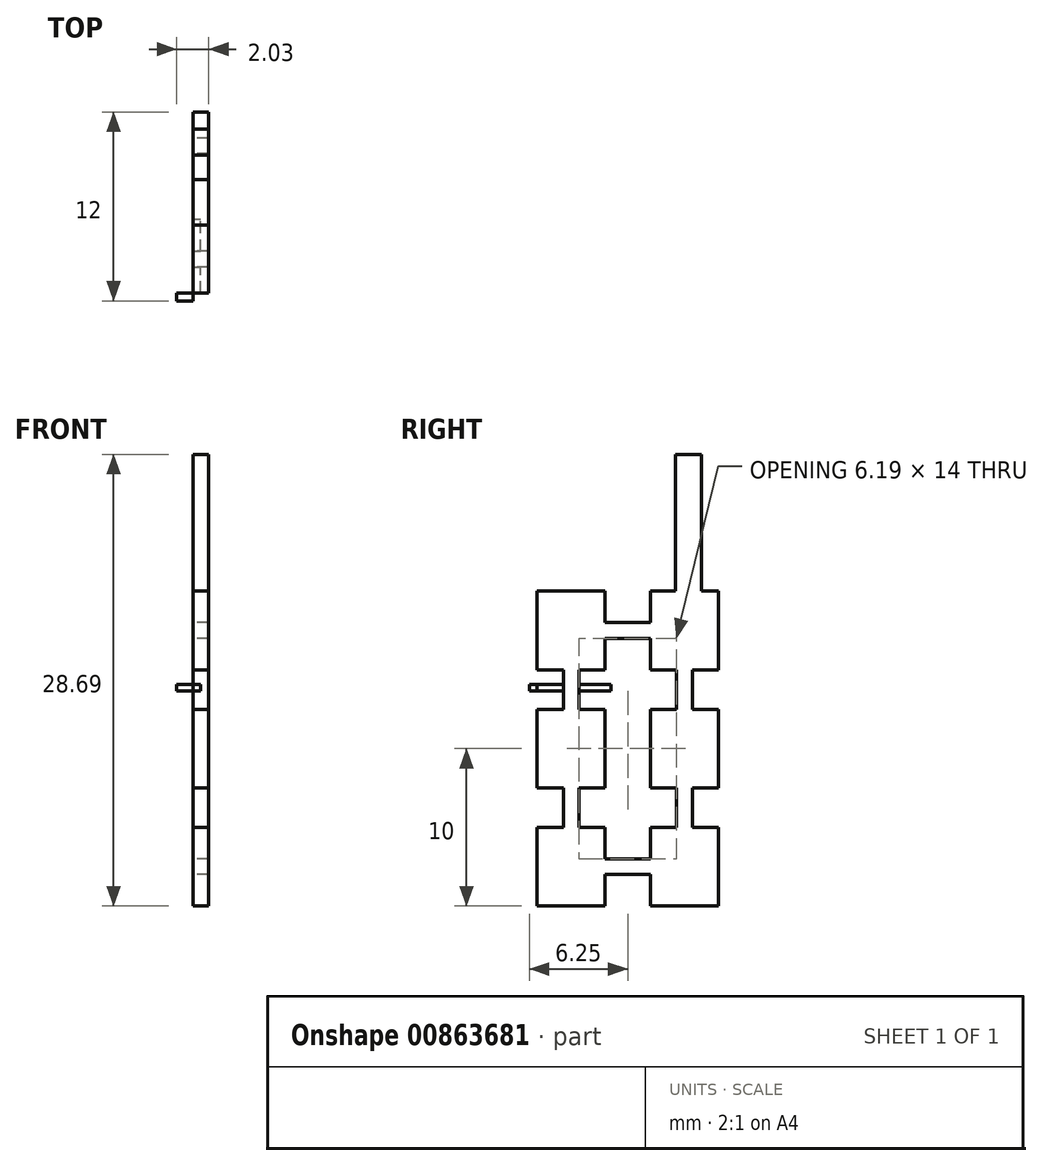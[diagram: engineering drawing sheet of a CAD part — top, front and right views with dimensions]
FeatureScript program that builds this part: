
annotation { "Feature Type Name" : "Feature", "Feature Type Description" : "" }
export const myFeature = defineFeature(function(context is Context, id is Id, definition is map)
    precondition{}
    {
        {
            var Q0;
            Q0=qCreatedBy(makeId("Right.planeOp"),FACE);
            var sketch = newSketch(context, id + "F0", { "sketchPlane" : qUnion([Q0])});
            skLineSegment(sketch, "E0.top", {"start": v(0, -11.5) * mm, "end": v(4.31, -11.5) * mm});
            skPoint(sketch, "E1.end.orphan", {"position": v(2.16, -7.19) * mm});
            skLineSegment(sketch, "E2", {"start": v(0, -11.5) * mm, "end": v(0, -6.5) * mm});
            skLineSegment(sketch, "E3", {"start": v(0, -6.5) * mm, "end": v(4.31, -6.5) * mm});
            skLineSegment(sketch, "E4.0", {"start": v(0, -4) * mm, "end": v(4.31, -4) * mm});
            skLineSegment(sketch, "E5.0", {"start": v(0, 1) * mm, "end": v(4.31, 1) * mm});
            skLineSegment(sketch, "E6.0", {"start": v(0, 3.5) * mm, "end": v(4.31, 3.5) * mm});
            skLineSegment(sketch, "E7.0", {"start": v(0, 8.5) * mm, "end": v(4.31, 8.5) * mm});
            skLineSegment(sketch, "E8", {"start": v(0, 8.5) * mm, "end": v(0, 3.5) * mm});
            skLineSegment(sketch, "E9", {"start": v(0, 1) * mm, "end": v(0, -4) * mm});
            skLineSegment(sketch, "E10", {"start": v(4.31, 8.5) * mm, "end": v(4.31, 3.5) * mm});
            skLineSegment(sketch, "E11", {"start": v(4.31, 1) * mm, "end": v(4.31, -4) * mm});
            skLineSegment(sketch, "E12.MirrorCS", {"start": v(11.5, 8.5) * mm, "end": v(7.19, 8.5) * mm});
            skLineSegment(sketch, "E13.MirrorCS", {"start": v(11.5, 8.5) * mm, "end": v(11.5, 3.5) * mm});
            skLineSegment(sketch, "E14.MirrorCS", {"start": v(11.5, 3.5) * mm, "end": v(7.19, 3.5) * mm});
            skLineSegment(sketch, "E15.MirrorCS", {"start": v(7.19, 8.5) * mm, "end": v(7.19, 3.5) * mm});
            skLineSegment(sketch, "E16.MirrorCS", {"start": v(11.5, 1) * mm, "end": v(7.19, 1) * mm});
            skLineSegment(sketch, "E17.MirrorCS", {"start": v(11.5, 1) * mm, "end": v(11.5, -4) * mm});
            skLineSegment(sketch, "E18.MirrorCS", {"start": v(11.5, -4) * mm, "end": v(7.19, -4) * mm});
            skLineSegment(sketch, "E19.MirrorCS", {"start": v(7.19, 1) * mm, "end": v(7.19, -4) * mm});
            skLineSegment(sketch, "E20.MirrorCS", {"start": v(11.5, -6.5) * mm, "end": v(7.19, -6.5) * mm});
            skLineSegment(sketch, "E21.MirrorCS", {"start": v(11.5, -11.5) * mm, "end": v(11.5, -6.5) * mm});
            skLineSegment(sketch, "E22.MirrorCS", {"start": v(11.5, -11.5) * mm, "end": v(7.19, -11.5) * mm});
            skLineSegment(sketch, "E23.MirrorCS", {"start": v(7.19, -7.19) * mm, "end": v(7.19, -11.5) * mm});
            skLineSegment(sketch, "E24.MirrorCS", {"start": v(7.19, -6.5) * mm, "end": v(7.19, -7.19) * mm});
            skLineSegment(sketch, "E25", {"start": v(4.31, -6.5) * mm, "end": v(4.31, -11.5) * mm});
            skLineSegment(sketch, "E26.0", {"start": v(4.31, -9.5) * mm, "end": v(7.19, -9.5) * mm});
            skLineSegment(sketch, "E27.0", {"start": v(4.31, -8.5) * mm, "end": v(7.19, -8.5) * mm});
            skLineSegment(sketch, "E28.0", {"start": v(8.84, -4) * mm, "end": v(8.84, -6.5) * mm});
            skLineSegment(sketch, "E29.0", {"start": v(9.84, -4) * mm, "end": v(9.84, -6.5) * mm});
            skLineSegment(sketch, "E30.0", {"start": v(1.66, -4) * mm, "end": v(1.66, -6.5) * mm});
            skLineSegment(sketch, "E31.0", {"start": v(2.66, -4) * mm, "end": v(2.66, -6.5) * mm});
            skLineSegment(sketch, "E32.0", {"start": v(1.66, 3.5) * mm, "end": v(1.66, 1) * mm});
            skLineSegment(sketch, "E33.0", {"start": v(2.66, 3.5) * mm, "end": v(2.66, 1) * mm});
            skLineSegment(sketch, "E34.0", {"start": v(4.31, 5.5) * mm, "end": v(7.19, 5.5) * mm});
            skLineSegment(sketch, "E35.0", {"start": v(4.31, 6.5) * mm, "end": v(7.19, 6.5) * mm});
            skLineSegment(sketch, "E36.0", {"start": v(8.84, 3.5) * mm, "end": v(8.84, 1) * mm});
            skLineSegment(sketch, "E37.0", {"start": v(9.84, 3.5) * mm, "end": v(9.84, 1) * mm});
            skPoint(sketch, "E38.end.orphan", {"position": v(2.16, -6.5) * mm});
            skPoint(sketch, "E38.start.orphan", {"position": v(2.16, -4) * mm});
            skPoint(sketch, "E39.start.orphan", {"position": v(4.31, -9) * mm});
            skPoint(sketch, "E40.end.orphan", {"position": v(9.34, -6.5) * mm});
            skPoint(sketch, "E40.start.orphan", {"position": v(9.34, -4) * mm});
            skPoint(sketch, "E41.end.orphan", {"position": v(9.34, 1) * mm});
            skPoint(sketch, "E41.start.orphan", {"position": v(9.34, 3.5) * mm});
            skPoint(sketch, "E42.end.orphan", {"position": v(7.19, 6) * mm});
            skPoint(sketch, "E42.start.orphan", {"position": v(4.31, 6) * mm});
            skPoint(sketch, "E43.end.orphan", {"position": v(2.16, 1) * mm});
            skPoint(sketch, "E43.start.orphan", {"position": v(2.16, 3.5) * mm});
            skLineSegment(sketch, "E44", {"start": v(10.42, 8.5) * mm, "end": v(10.42, 17.2) * mm});
            skLineSegment(sketch, "E45", {"start": v(10.42, 17.2) * mm, "end": v(8.77, 17.2) * mm});
            skLineSegment(sketch, "E46", {"start": v(8.77, 17.2) * mm, "end": v(8.77, 8.5) * mm});
            skSolve(sketch);
        }
        {
            var Q0;
            {var subQ0=sQuery(id+"F0.wireOp",EDGE,"E7.0");Q0=makeQuery(id+"F0.imprint","IMPRINT",FACE,{"disambiguationData":[TD([[makeQuery(id+"F0.imprint","IMPRINT",EDGE,{"derivedFrom":subQ0}),-1.0]])]});}
            var Q1;
            {var subQ0=sQuery(id+"F0.wireOp",EDGE,"E32.0");Q1=makeQuery(id+"F0.imprint","IMPRINT",FACE,{"disambiguationData":[TD([[makeQuery(id+"F0.imprint","IMPRINT",EDGE,{"derivedFrom":subQ0}),1.0]])]});}
            var Q2;
            {var subQ0=sQuery(id+"F0.wireOp",EDGE,"E9");Q2=makeQuery(id+"F0.imprint","IMPRINT",FACE,{"disambiguationData":[TD([[makeQuery(id+"F0.imprint","IMPRINT",EDGE,{"derivedFrom":subQ0}),1.0]])]});}
            var Q3;
            {var subQ0=sQuery(id+"F0.wireOp",EDGE,"E30.0");Q3=makeQuery(id+"F0.imprint","IMPRINT",FACE,{"disambiguationData":[TD([[makeQuery(id+"F0.imprint","IMPRINT",EDGE,{"derivedFrom":subQ0}),1.0]])]});}
            var Q4;
            {var subQ7=sQuery(id+"F0.wireOp",EDGE,"E2");Q4=makeQuery(id+"F0.imprint","IMPRINT",FACE,{"disambiguationData":[TD([[makeQuery(id+"F0.imprint","IMPRINT",EDGE,{"derivedFrom":subQ7}),-1.0]])]});}
            var Q5;
            {var subQ0=sQuery(id+"F0.wireOp",EDGE,"E26.0");Q5=makeQuery(id+"F0.imprint","IMPRINT",FACE,{"disambiguationData":[TD([[makeQuery(id+"F0.imprint","IMPRINT",EDGE,{"derivedFrom":subQ0}),1.0]])]});}
            var Q6;
            {var subQ0=sQuery(id+"F0.wireOp",EDGE,"E21.MirrorCS");Q6=makeQuery(id+"F0.imprint","IMPRINT",FACE,{"disambiguationData":[TD([[makeQuery(id+"F0.imprint","IMPRINT",EDGE,{"derivedFrom":subQ0}),1.0]])]});}
            var Q7;
            {var subQ0=sQuery(id+"F0.wireOp",EDGE,"E28.0");Q7=makeQuery(id+"F0.imprint","IMPRINT",FACE,{"disambiguationData":[TD([[makeQuery(id+"F0.imprint","IMPRINT",EDGE,{"derivedFrom":subQ0}),1.0]])]});}
            var Q8;
            {var subQ0=sQuery(id+"F0.wireOp",EDGE,"E17.MirrorCS");Q8=makeQuery(id+"F0.imprint","IMPRINT",FACE,{"disambiguationData":[TD([[makeQuery(id+"F0.imprint","IMPRINT",EDGE,{"derivedFrom":subQ0}),-1.0]])]});}
            var Q9;
            {var subQ4=sQuery(id+"F0.wireOp",EDGE,"E12.MirrorCS");Q9=makeQuery(id+"F0.imprint","IMPRINT",FACE,{"disambiguationData":[TD([[makeQuery(id+"F0.imprint","IMPRINT",EDGE,{"derivedFrom":subQ4}),1.0]])]});}
            var Q10;
            {var subQ0=sQuery(id+"F0.wireOp",EDGE,"E34.0");Q10=makeQuery(id+"F0.imprint","IMPRINT",FACE,{"disambiguationData":[TD([[makeQuery(id+"F0.imprint","IMPRINT",EDGE,{"derivedFrom":subQ0}),1.0]])]});}
            var Q11;
            {var subQ0=sQuery(id+"F0.wireOp",EDGE,"E36.0");Q11=makeQuery(id+"F0.imprint","IMPRINT",FACE,{"disambiguationData":[TD([[makeQuery(id+"F0.imprint","IMPRINT",EDGE,{"derivedFrom":subQ0}),1.0]])]});}
            var Q12;
            {var subQ0=sQuery(id+"F0.wireOp",EDGE,"E44");Q12=makeQuery(id+"F0.imprint","IMPRINT",FACE,{"disambiguationData":[TD([[makeQuery(id+"F0.imprint","IMPRINT",EDGE,{"derivedFrom":subQ0}),1.0]])]});}
            extrude(context, id + "F1", {"entities" : qUnion([Q0, Q1, Q2, Q3, Q4, Q5, Q6, Q7, Q8, Q9, Q10, Q11, Q12]), "depth" : 1 * mm, "offsetDistance" : 25 * mm});
        }
        {
            var Q0;
            Q0=qCreatedBy(makeId("Right.planeOp"),FACE);
            var sketch = newSketch(context, id + "F2", { "sketchPlane" : qUnion([Q0])});
            skLineSegment(sketch, "E47.bottom", {"start": v(0, 2.58) * mm, "end": v(4.68, 2.58) * mm});
            skLineSegment(sketch, "E47.top", {"start": v(0, 2.17) * mm, "end": v(4.68, 2.17) * mm});
            skLineSegment(sketch, "E47.left", {"start": v(0, 2.58) * mm, "end": v(0, 2.17) * mm});
            skLineSegment(sketch, "E47.right", {"start": v(4.68, 2.58) * mm, "end": v(4.68, 2.17) * mm});
            skSolve(sketch);
        }
        {
            var Q0;
            Q0=makeQuery(id+"F2.imprint","IMPRINT",FACE,{"disambiguationData":[TD([[makeQuery(id+"F2.imprint","IMPRINT",EDGE,{"derivedFrom":sQuery(id+"F2.wireOp",EDGE,"E47.bottom")}),-1.0]])]});
            extrude(context, id + "F3", {"entities" : qUnion([Q0]), "operationType" : NewBodyOperationType.ADD, "depth" : .5 * mm, "offsetDistance" : 25 * mm});
        }
        {
            var Q0;
            Q0=qCreatedBy(makeId("Front.planeOp"),FACE);
            var sketch = newSketch(context, id + "F4", { "sketchPlane" : qUnion([Q0])});
            skLineSegment(sketch, "E48.0", {"start": v(0, 2.58) * mm, "end": v(0, 2.17) * mm});
            skLineSegment(sketch, "E49", {"start": v(0, 2.58) * mm, "end": v(-1.03, 2.58) * mm});
            skLineSegment(sketch, "E50", {"start": v(-1.03, 2.58) * mm, "end": v(-1.03, 2.17) * mm});
            skLineSegment(sketch, "E51", {"start": v(-1.03, 2.17) * mm, "end": v(0, 2.17) * mm});
            skSolve(sketch);
        }
        {
            var Q0;
            Q0=makeQuery(id+"F4.imprint","IMPRINT",FACE,{"disambiguationData":[TD([[makeQuery(id+"F4.imprint","IMPRINT",EDGE,{"derivedFrom":sQuery(id+"F4.wireOp",EDGE,"E48.0")}),-1.0]])]});
            extrude(context, id + "F5", {"entities" : qUnion([Q0]), "depth" : .5 * mm, "offsetDistance" : 25 * mm});
        }
    });
